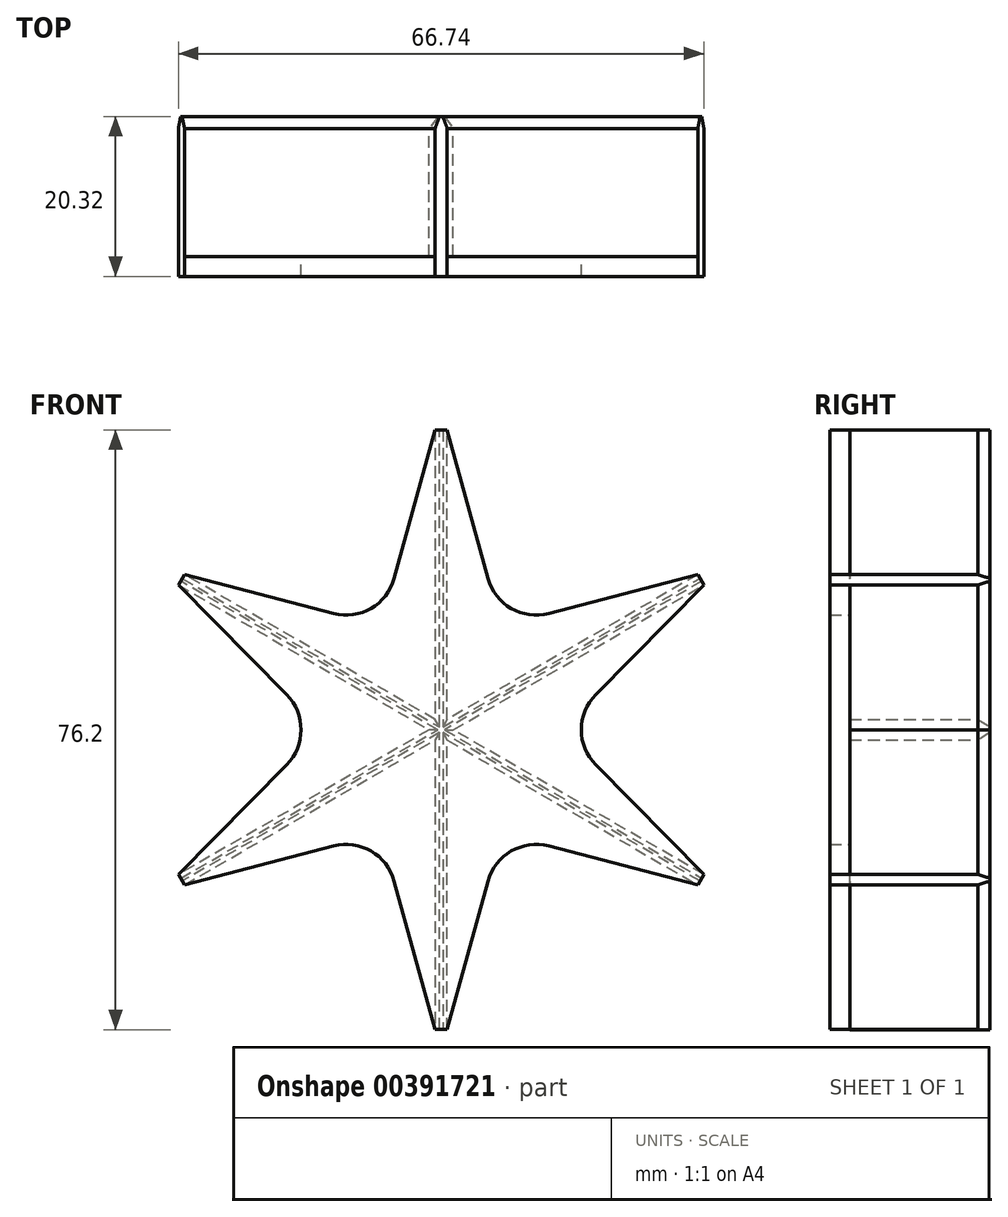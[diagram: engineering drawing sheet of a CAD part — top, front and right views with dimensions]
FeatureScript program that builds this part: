
annotation { "Feature Type Name" : "Feature", "Feature Type Description" : "" }
export const myFeature = defineFeature(function(context is Context, id is Id, definition is map)
    precondition{}
    {
        {
            var Q0;
            Q0=qCreatedBy(makeId("Front.planeOp"),FACE);
            var sketch = newSketch(context, id + "F0", { "sketchPlane" : qUnion([Q0])});
            skArc(sketch, "E0", {"start": v(0.76, 38.1) * mm, "mid": v(0, 38.1) * mm, "end": v(-0.76, 38.1) * mm});
            skLineSegment(sketch, "E1", {"start": v(-0.76, 38.1) * mm, "end": v(-0.76, 1.32) * mm});
            skLineSegment(sketch, "E2", {"start": v(0.76, -38.1) * mm, "end": v(0.76, -1.32) * mm});
            skLineSegment(sketch, "E3", {"start": v(32.6, 19.7) * mm, "end": v(0.76, 1.32) * mm});
            skLineSegment(sketch, "E4", {"start": v(-32.6, -19.7) * mm, "end": v(-0.76, -1.32) * mm});
            skLineSegment(sketch, "E5", {"start": v(33.37, -18.39) * mm, "end": v(1.52, 0) * mm});
            skLineSegment(sketch, "E6", {"start": v(-33.37, 18.39) * mm, "end": v(-1.52, 0) * mm});
            skArc(sketch, "E7.trimOffspring", {"start": v(-32.6, 19.7) * mm, "mid": v(-33, 19.05) * mm, "end": v(-33.37, 18.39) * mm});
            skArc(sketch, "E8.trimOffspring", {"start": v(-33.37, -18.39) * mm, "mid": v(-33, -19.05) * mm, "end": v(-32.6, -19.7) * mm});
            skArc(sketch, "E9.trimOffspring", {"start": v(-0.76, -38.1) * mm, "mid": v(0, -38.1) * mm, "end": v(0.76, -38.1) * mm});
            skArc(sketch, "E10.trimOffspring", {"start": v(32.6, -19.7) * mm, "mid": v(33, -19.05) * mm, "end": v(33.37, -18.39) * mm});
            skArc(sketch, "E11.trimOffspring", {"start": v(33.37, 18.39) * mm, "mid": v(33, 19.05) * mm, "end": v(32.6, 19.7) * mm});
            skLineSegment(sketch, "E12.trimOffspring", {"start": v(1.52, 0) * mm, "end": v(33.37, 18.39) * mm});
            skLineSegment(sketch, "E13.trimOffspring", {"start": v(-0.76, 1.32) * mm, "end": v(-32.6, 19.7) * mm});
            skLineSegment(sketch, "E14.trimOffspring", {"start": v(0.76, 1.32) * mm, "end": v(0.76, 38.1) * mm});
            skLineSegment(sketch, "E15.trimOffspring", {"start": v(-1.52, 0) * mm, "end": v(-33.37, -18.39) * mm});
            skLineSegment(sketch, "E16.trimOffspring", {"start": v(0.76, -1.32) * mm, "end": v(32.6, -19.7) * mm});
            skLineSegment(sketch, "E17.trimOffspring", {"start": v(-0.76, -1.32) * mm, "end": v(-0.76, -38.1) * mm});
            skSolve(sketch);
        }
        {
            var Q0;
            Q0 = qSketchRegion(id + "F0", true);
            extrude(context, id + "F1", {"entities" : qUnion([Q0]), "depth" : 17.78 * mm});
        }
        {
            var Q0;
            Q0=makeQuery(id+"F1.opExtrude","CAP_FACE",FACE,{"disambiguationData":[OSD([sQuery(id+"F0.wireOp",EDGE,"E0"),sQuery(id+"F0.wireOp",EDGE,"E1"),sQuery(id+"F0.wireOp",EDGE,"E2"),sQuery(id+"F0.wireOp",EDGE,"E3"),sQuery(id+"F0.wireOp",EDGE,"E4"),sQuery(id+"F0.wireOp",EDGE,"E5"),sQuery(id+"F0.wireOp",EDGE,"E6"),sQuery(id+"F0.wireOp",EDGE,"E7.trimOffspring"),sQuery(id+"F0.wireOp",EDGE,"E8.trimOffspring"),sQuery(id+"F0.wireOp",EDGE,"E9.trimOffspring"),sQuery(id+"F0.wireOp",EDGE,"E10.trimOffspring"),sQuery(id+"F0.wireOp",EDGE,"E11.trimOffspring"),sQuery(id+"F0.wireOp",EDGE,"E12.trimOffspring"),sQuery(id+"F0.wireOp",EDGE,"E13.trimOffspring"),sQuery(id+"F0.wireOp",EDGE,"E14.trimOffspring"),sQuery(id+"F0.wireOp",EDGE,"E15.trimOffspring"),sQuery(id+"F0.wireOp",EDGE,"E16.trimOffspring"),sQuery(id+"F0.wireOp",EDGE,"E17.trimOffspring")])],"isStart":false});
            var sketch = newSketch(context, id + "F2", { "sketchPlane" : qUnion([Q0])});
            skLineSegment(sketch, "E18", {"start": v(-0.76, 38.1) * mm, "end": v(0.76, 38.1) * mm});
            skLineSegment(sketch, "E19", {"start": v(0.76, 38.1) * mm, "end": v(5.96, 19.23) * mm});
            skLineSegment(sketch, "E20", {"start": v(13.68, 14.78) * mm, "end": v(32.6, 19.7) * mm});
            skLineSegment(sketch, "E21", {"start": v(32.6, 19.7) * mm, "end": v(33.37, 18.39) * mm});
            skLineSegment(sketch, "E22", {"start": v(33.37, 18.39) * mm, "end": v(19.64, 4.46) * mm});
            skLineSegment(sketch, "E23", {"start": v(19.64, -4.46) * mm, "end": v(33.37, -18.39) * mm});
            skLineSegment(sketch, "E24", {"start": v(33.37, -18.39) * mm, "end": v(32.6, -19.7) * mm});
            skLineSegment(sketch, "E25", {"start": v(32.6, -19.7) * mm, "end": v(13.68, -14.78) * mm});
            skLineSegment(sketch, "E26", {"start": v(5.96, -19.23) * mm, "end": v(0.76, -38.1) * mm});
            skLineSegment(sketch, "E27", {"start": v(0.76, -38.1) * mm, "end": v(-0.76, -38.1) * mm});
            skLineSegment(sketch, "E28", {"start": v(-0.76, -38.1) * mm, "end": v(-5.96, -19.23) * mm});
            skLineSegment(sketch, "E29", {"start": v(-13.68, -14.78) * mm, "end": v(-32.6, -19.7) * mm});
            skLineSegment(sketch, "E30", {"start": v(-32.6, -19.7) * mm, "end": v(-33.37, -18.39) * mm});
            skLineSegment(sketch, "E31", {"start": v(-33.37, -18.39) * mm, "end": v(-19.64, -4.46) * mm});
            skLineSegment(sketch, "E32", {"start": v(-19.64, 4.46) * mm, "end": v(-33.37, 18.39) * mm});
            skLineSegment(sketch, "E33", {"start": v(-33.37, 18.39) * mm, "end": v(-32.6, 19.7) * mm});
            skLineSegment(sketch, "E34", {"start": v(-32.6, 19.7) * mm, "end": v(-13.68, 14.78) * mm});
            skLineSegment(sketch, "E35", {"start": v(-5.96, 19.23) * mm, "end": v(-0.76, 38.1) * mm});
            skLineSegment(sketch, "E36", {"start": v(0, 0) * mm, "end": v(7.62, 13.2) * mm, "construction": true});
            skLineSegment(sketch, "E37", {"start": v(0, 0) * mm, "end": v(-7.62, 13.2) * mm, "construction": true});
            skLineSegment(sketch, "E38", {"start": v(0, 0) * mm, "end": v(7.62, -13.2) * mm, "construction": true});
            skLineSegment(sketch, "E39", {"start": v(0, 0) * mm, "end": v(-7.62, -13.2) * mm, "construction": true});
            skPoint(sketch, "E40.visualSharp", {"position": v(7.62, 13.2) * mm});
            skArc(sketch, "E40.filletArc", {"start": v(5.96, 19.23) * mm, "mid": v(8.9, 15.42) * mm, "end": v(13.68, 14.78) * mm});
            skPoint(sketch, "E41.visualSharp", {"position": v(15.24, 0) * mm});
            skArc(sketch, "E41.filletArc", {"start": v(19.64, 4.46) * mm, "mid": v(17.8, 0) * mm, "end": v(19.64, -4.46) * mm});
            skPoint(sketch, "E42.visualSharp", {"position": v(7.62, -13.2) * mm});
            skArc(sketch, "E42.filletArc", {"start": v(13.68, -14.78) * mm, "mid": v(8.9, -15.42) * mm, "end": v(5.96, -19.23) * mm});
            skPoint(sketch, "E43.visualSharp", {"position": v(-7.62, -13.2) * mm});
            skArc(sketch, "E43.filletArc", {"start": v(-5.96, -19.23) * mm, "mid": v(-8.9, -15.42) * mm, "end": v(-13.68, -14.78) * mm});
            skPoint(sketch, "E44.visualSharp", {"position": v(-15.24, 0) * mm});
            skArc(sketch, "E44.filletArc", {"start": v(-19.64, -4.46) * mm, "mid": v(-17.8, 0) * mm, "end": v(-19.64, 4.46) * mm});
            skPoint(sketch, "E45.visualSharp", {"position": v(-7.62, 13.2) * mm});
            skArc(sketch, "E45.filletArc", {"start": v(-13.68, 14.78) * mm, "mid": v(-8.9, 15.42) * mm, "end": v(-5.96, 19.23) * mm});
            skSolve(sketch);
        }
        {
            var Q0;
            Q0 = qSketchRegion(id + "F2", true);
            extrude(context, id + "F3", {"entities" : qUnion([Q0]), "operationType" : NewBodyOperationType.ADD, "depth" : 2.54 * mm});
        }
        {
            var Q0;
            Q0=makeQuery(id+"F1.opExtrude","CAP_EDGE",EDGE,{"disambiguationData":[OSD([sQuery(id+"F0.wireOp",EDGE,"E14.trimOffspring")])],"isStart":true});
            var Q1;
            Q1=makeQuery(id+"F1.opExtrude","CAP_EDGE",EDGE,{"disambiguationData":[OSD([sQuery(id+"F0.wireOp",EDGE,"E1")])],"isStart":true});
            var Q2;
            Q2=makeQuery(id+"F1.opExtrude","CAP_EDGE",EDGE,{"disambiguationData":[OSD([sQuery(id+"F0.wireOp",EDGE,"E13.trimOffspring")])],"isStart":true});
            var Q3;
            Q3=makeQuery(id+"F1.opExtrude","CAP_EDGE",EDGE,{"disambiguationData":[OSD([sQuery(id+"F0.wireOp",EDGE,"E6")])],"isStart":true});
            var Q4;
            Q4=makeQuery(id+"F1.opExtrude","CAP_EDGE",EDGE,{"disambiguationData":[OSD([sQuery(id+"F0.wireOp",EDGE,"E15.trimOffspring")])],"isStart":true});
            var Q5;
            Q5=makeQuery(id+"F1.opExtrude","CAP_EDGE",EDGE,{"disambiguationData":[OSD([sQuery(id+"F0.wireOp",EDGE,"E4")])],"isStart":true});
            var Q6;
            Q6=makeQuery(id+"F1.opExtrude","CAP_EDGE",EDGE,{"disambiguationData":[OSD([sQuery(id+"F0.wireOp",EDGE,"E17.trimOffspring")])],"isStart":true});
            var Q7;
            Q7=makeQuery(id+"F1.opExtrude","CAP_EDGE",EDGE,{"disambiguationData":[OSD([sQuery(id+"F0.wireOp",EDGE,"E2")])],"isStart":true});
            var Q8;
            Q8=makeQuery(id+"F1.opExtrude","CAP_EDGE",EDGE,{"disambiguationData":[OSD([sQuery(id+"F0.wireOp",EDGE,"E16.trimOffspring")])],"isStart":true});
            var Q9;
            Q9=makeQuery(id+"F1.opExtrude","CAP_EDGE",EDGE,{"disambiguationData":[OSD([sQuery(id+"F0.wireOp",EDGE,"E5")])],"isStart":true});
            var Q10;
            Q10=makeQuery(id+"F1.opExtrude","CAP_EDGE",EDGE,{"disambiguationData":[OSD([sQuery(id+"F0.wireOp",EDGE,"E12.trimOffspring")])],"isStart":true});
            var Q11;
            Q11=makeQuery(id+"F1.opExtrude","CAP_EDGE",EDGE,{"disambiguationData":[OSD([sQuery(id+"F0.wireOp",EDGE,"E3")])],"isStart":true});
            chamfer(context, id + "F4", {"entities" : qUnion([Q0, Q1, Q2, Q3, Q4, Q5, Q6, Q7, Q8, Q9, Q10, Q11]), "chamferType" : ChamferType.OFFSET_ANGLE, "width" : 1.52 * mm, "oppositeDirection" : false, "angle" : 20 * degree, "tangentPropagation" : true});
        }
    });
